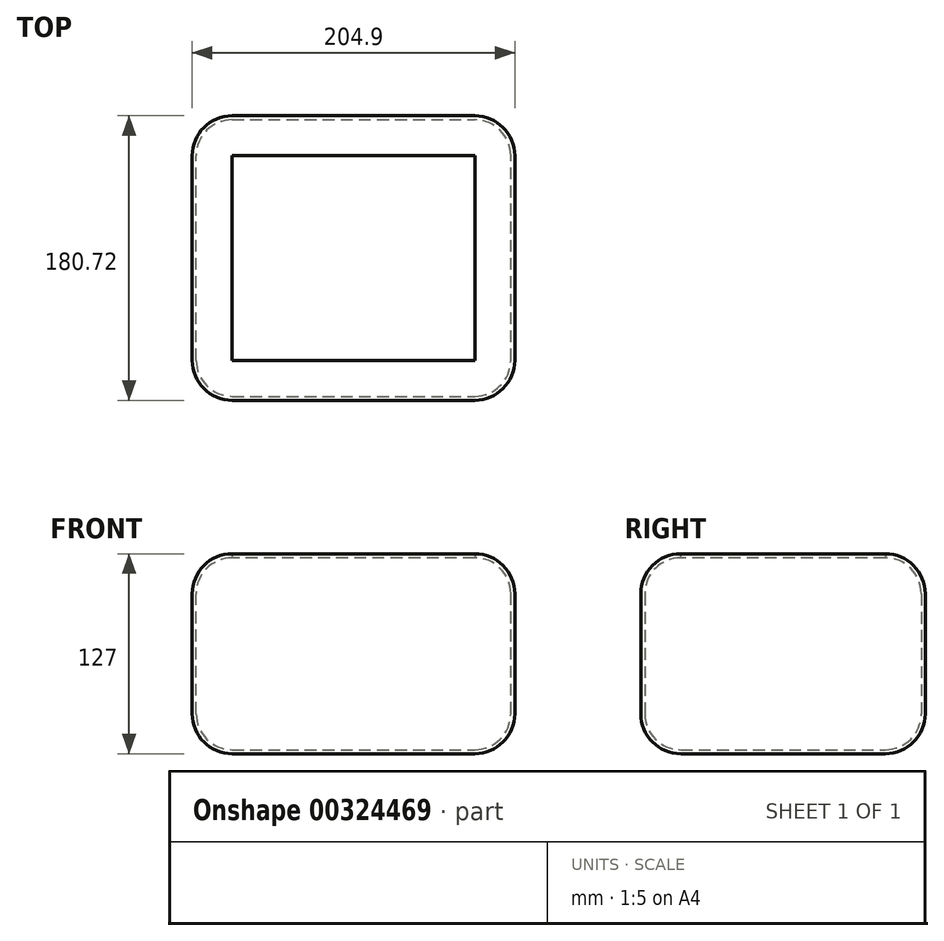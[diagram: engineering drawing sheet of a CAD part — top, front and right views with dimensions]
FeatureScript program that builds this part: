
annotation { "Feature Type Name" : "Feature", "Feature Type Description" : "" }
export const myFeature = defineFeature(function(context is Context, id is Id, definition is map)
    precondition{}
    {
        {
            var Q0;
            Q0=qCreatedBy(makeId("Top.planeOp"),FACE);
            var sketch = newSketch(context, id + "F0", { "sketchPlane" : qUnion([Q0])});
            skLineSegment(sketch, "E0.bottom", {"start": v(102.45, -90.36) * mm, "end": v(-102.45, -90.36) * mm});
            skLineSegment(sketch, "E0.top", {"start": v(102.45, 90.36) * mm, "end": v(-102.45, 90.36) * mm});
            skLineSegment(sketch, "E0.left", {"start": v(102.45, -90.36) * mm, "end": v(102.45, 90.36) * mm});
            skLineSegment(sketch, "E0.right", {"start": v(-102.45, -90.36) * mm, "end": v(-102.45, 90.36) * mm});
            skPoint(sketch, "E0.middle", {"position": v(0, 0) * mm});
            skSolve(sketch);
        }
        {
            var Q0;
            Q0 = qSketchRegion(id + "F0", true);
            extrude(context, id + "F1", {"entities" : qUnion([Q0]), "depth" : 127 * mm});
        }
        {
            var Q0;
            Q0=makeQuery(id+"F1.opExtrude","SWEPT_FACE",FACE,{"disambiguationData":[OSD([sQuery(id+"F0.wireOp",EDGE,"E0.bottom")])]});
            var Q1;
            Q1=makeQuery(id+"F1.opExtrude","SWEPT_FACE",FACE,{"disambiguationData":[OSD([sQuery(id+"F0.wireOp",EDGE,"E0.left")])]});
            var Q2;
            Q2=makeQuery(id+"F1.opExtrude","CAP_FACE",FACE,{"disambiguationData":[OSD([sQuery(id+"F0.wireOp",EDGE,"E0.bottom"),sQuery(id+"F0.wireOp",EDGE,"E0.top"),sQuery(id+"F0.wireOp",EDGE,"E0.left"),sQuery(id+"F0.wireOp",EDGE,"E0.right")])],"isStart":false});
            var Q3;
            Q3=makeQuery(id+"F1.opExtrude","SWEPT_FACE",FACE,{"disambiguationData":[OSD([sQuery(id+"F0.wireOp",EDGE,"E0.right")])]});
            var Q4;
            Q4=makeQuery(id+"F1.opExtrude","SWEPT_FACE",FACE,{"disambiguationData":[OSD([sQuery(id+"F0.wireOp",EDGE,"E0.top")])]});
            var Q5;
            Q5=makeQuery(id+"F1.opExtrude","CAP_FACE",FACE,{"disambiguationData":[OSD([sQuery(id+"F0.wireOp",EDGE,"E0.bottom"),sQuery(id+"F0.wireOp",EDGE,"E0.top"),sQuery(id+"F0.wireOp",EDGE,"E0.left"),sQuery(id+"F0.wireOp",EDGE,"E0.right")])],"isStart":true});
            fillet(context, id + "F2", {"entities" : qUnion([Q0, Q1, Q2, Q3, Q4, Q5]), "radius" : 25.4 * mm, "tangentPropagation" : true, "allowEdgeOverflow" : false});
        }
        {
            var Q0;
            Q0=makeQuery(id+"F1.opExtrude","CAP_FACE",FACE,{"disambiguationData":[OSD([sQuery(id+"F0.wireOp",EDGE,"E0.bottom"),sQuery(id+"F0.wireOp",EDGE,"E0.top"),sQuery(id+"F0.wireOp",EDGE,"E0.left"),sQuery(id+"F0.wireOp",EDGE,"E0.right")])],"isStart":false});
            shell(context, id + "F3", {"entities" : qUnion([Q0]), "thickness" : 2.54 * mm});
        }
    });
